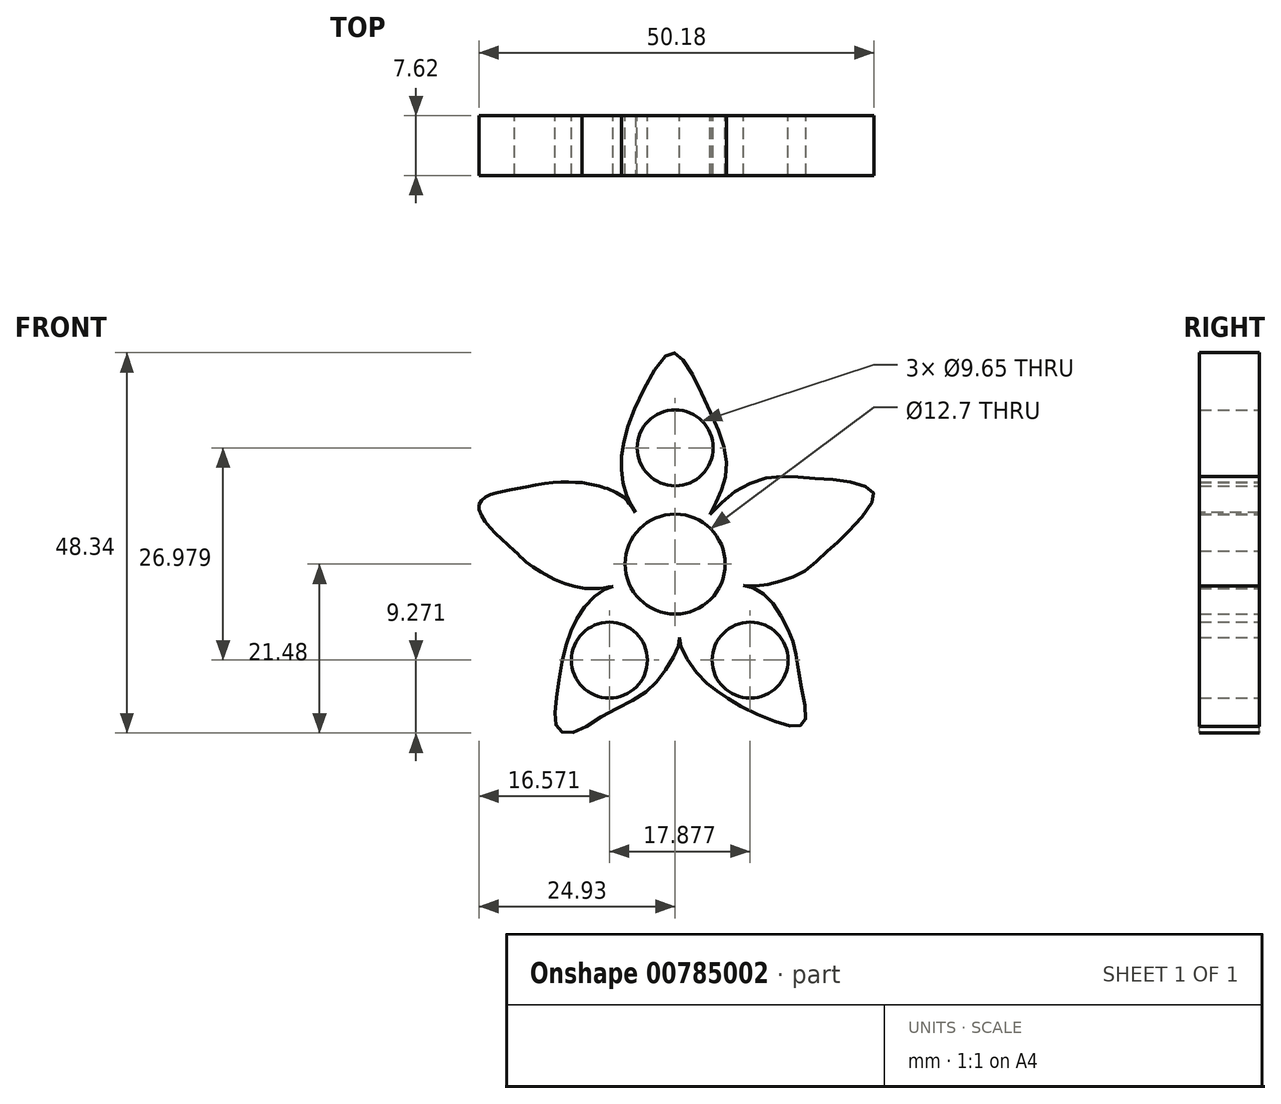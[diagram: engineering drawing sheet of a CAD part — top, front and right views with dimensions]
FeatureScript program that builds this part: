
annotation { "Feature Type Name" : "Feature", "Feature Type Description" : "" }
export const myFeature = defineFeature(function(context is Context, id is Id, definition is map)
    precondition{}
    {
        {
            var Q0;
            Q0=qCreatedBy(makeId("Front.planeOp"),FACE);
            var sketch = newSketch(context, id + "F0", { "sketchPlane" : qUnion([Q0])});
            skFitSpline(sketch, "E0", {"points": [v(4.4, 6.28) * mm, v(6, 9.65) * mm, v(6.47, 13.59) * mm, v(4.22, 19.87) * mm, v(0.75, 26.24) * mm, v(-0.84, 26.7) * mm, v(-4.87, 20.33) * mm, v(-6.65, 14.8) * mm, v(-6.75, 10.96) * mm, v(-5.9, 8.06) * mm, v(-5.06, 6.56) * mm], "startDerivative": vector(18.97, 35.24) * mm, "endDerivative": vector(13.54, -21.4) * mm});
            skFitSpline(sketch, "E1", {"points": [v(-5.06, 6.56) * mm, v(-6.82, 8.68) * mm, v(-9.68, 9.9) * mm, v(-11.83, 10.35) * mm], "startDerivative": vector(-4.4, 6.87) * mm, "endDerivative": vector(-6.72, 1.19) * mm});
            skFitSpline(sketch, "E2", {"points": [v(-11.83, 10.35) * mm, v(-15.47, 10.35) * mm, v(-20.88, 9.44) * mm, v(-23.66, 8.71) * mm, v(-24.9, 7.52) * mm, v(-23.95, 5.15) * mm, v(-20.38, 1.66) * mm], "startDerivative": vector(-19.58, 1.1) * mm, "endDerivative": vector(19.68, -17.17) * mm});
            skFitSpline(sketch, "E3", {"points": [v(-20.38, 1.66) * mm, v(-18.56, 0) * mm, v(-15.45, -1.87) * mm, v(-11.3, -3.1) * mm, v(-7.88, -2.82) * mm], "startDerivative": vector(7.95, -7.89) * mm, "endDerivative": vector(13.3, 2.3) * mm});
            skFitSpline(sketch, "E4", {"points": [v(-7.88, -2.82) * mm, v(-9.46, -3.49) * mm, v(-11.83, -5.85) * mm, v(-13.4, -8.88) * mm, v(-14.61, -13.8) * mm, v(-15.25, -18.88) * mm, v(-14.9, -21) * mm, v(-13, -21.4) * mm, v(-8.95, -19.14) * mm, v(-4.25, -16.67) * mm, v(-1.57, -13.87) * mm, v(0.32, -10.8) * mm, v(0.55, -9.3) * mm], "startDerivative": vector(-25.43, -7.66) * mm, "endDerivative": vector(0.7, 24.6) * mm});
            skFitSpline(sketch, "E5", {"points": [v(0.55, -9.3) * mm, v(0.87, -10.8) * mm, v(3.15, -14.3) * mm, v(5.4, -16.16) * mm, v(8.22, -18) * mm, v(13.36, -20.24) * mm, v(15.87, -20.5) * mm, v(16.57, -19.68) * mm, v(15.98, -15.6) * mm, v(15.24, -11.03) * mm, v(14.38, -8.38) * mm, v(12.47, -5.12) * mm, v(10.49, -3.3) * mm, v(8.66, -2.7) * mm], "startDerivative": vector(1.98, -24.24) * mm, "endDerivative": vector(-30.25, 6.85) * mm});
            skFitSpline(sketch, "E6", {"points": [v(8.66, -2.7) * mm, v(11.08, -2.7) * mm, v(13.9, -2) * mm, v(16.47, -0.84) * mm, v(19.32, 1.62) * mm, v(21.77, 3.87) * mm, v(25.11, 8.1) * mm, v(24.97, 9.32) * mm, v(21.93, 10.5) * mm, v(16.73, 10.96) * mm, v(12.32, 11.06) * mm, v(8.01, 9.46) * mm, v(4.4, 6.28) * mm], "startDerivative": vector(34.48, -2.17) * mm, "endDerivative": vector(-35.06, -35.98) * mm});
            skCircle(sketch, "E7", {"center": v(0, 0) * mm, "radius": 6.35 * mm});
            skCircle(sketch, "E8", {"center": v(0, 14.77) * mm, "radius": 4.83 * mm});
            skCircle(sketch, "E9", {"center": v(-8.36, -12.2) * mm, "radius": 4.83 * mm});
            skCircle(sketch, "E10", {"center": v(9.52, -12.2) * mm, "radius": 4.83 * mm});
            skSolve(sketch);
        }
        {
            var Q0;
            Q0 = qSketchRegion(id + "F0", true);
            extrude(context, id + "F1", {"entities" : qUnion([Q0]), "depth" : 7.62 * mm, "offsetDistance" : 25.4 * mm});
        }
    });
